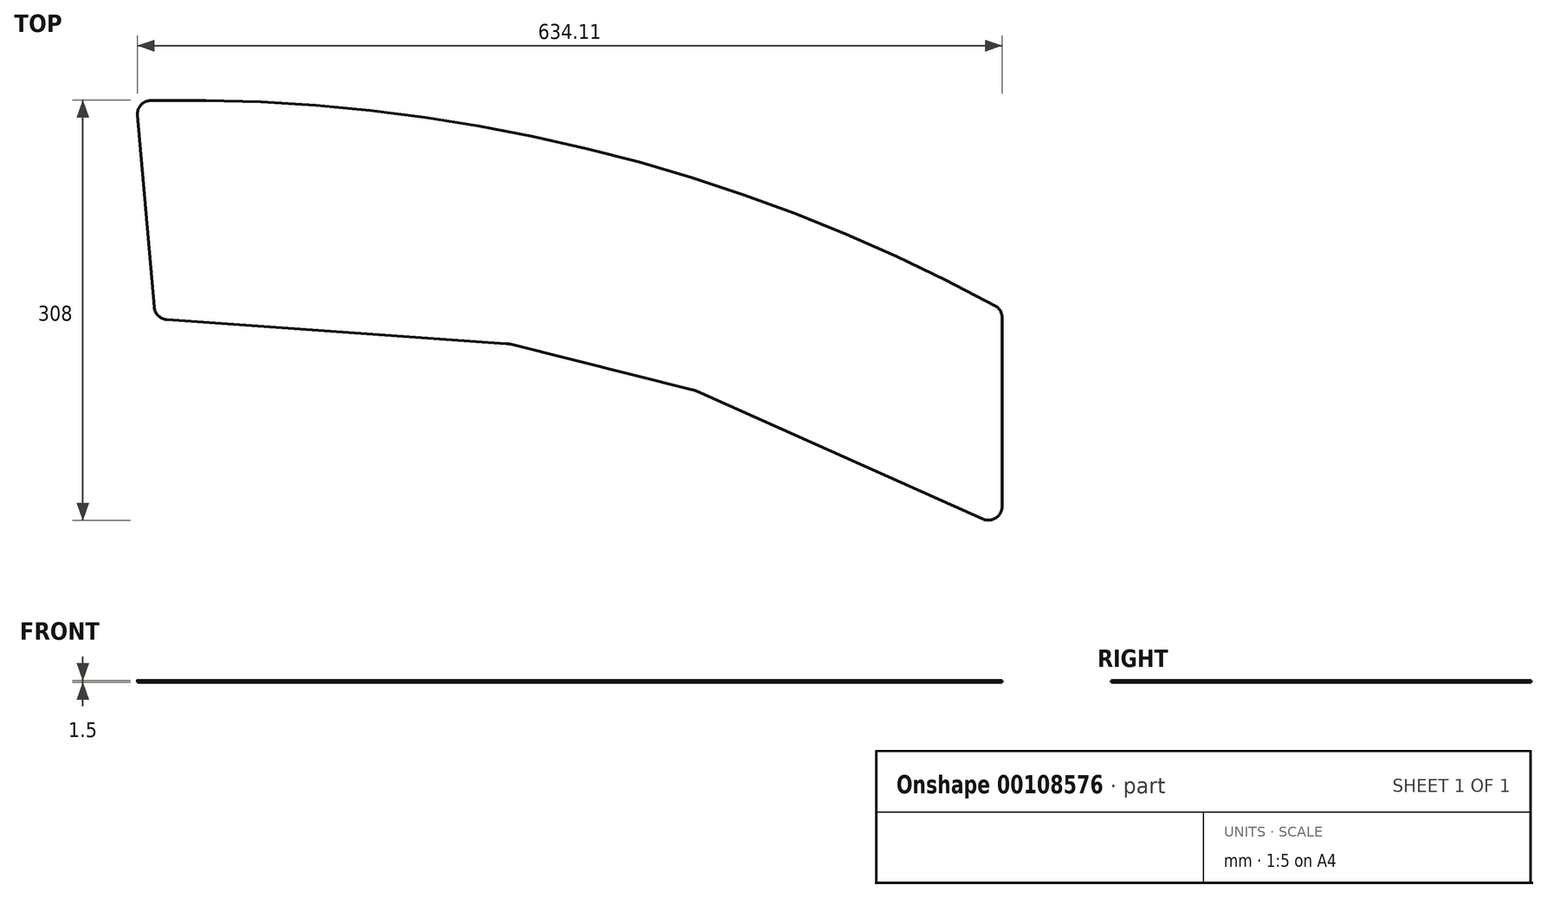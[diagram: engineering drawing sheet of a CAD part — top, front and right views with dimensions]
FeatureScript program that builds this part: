
annotation { "Feature Type Name" : "Feature", "Feature Type Description" : "" }
export const myFeature = defineFeature(function(context is Context, id is Id, definition is map)
    precondition{}
    {
        {
            var Q0;
            Q0=qCreatedBy(makeId("Top.planeOp"),FACE);
            var sketch = newSketch(context, id + "F0", { "sketchPlane" : qUnion([Q0])});
            skLineSegment(sketch, "E0", {"start": v(0, 450) * mm, "end": v(-635, 450) * mm});
            skLineSegment(sketch, "E1", {"start": v(-635, 450) * mm, "end": v(-635, 0) * mm});
            skLineSegment(sketch, "E2", {"start": v(-635, 0) * mm, "end": v(0, 0) * mm});
            skLineSegment(sketch, "E3", {"start": v(0, 0) * mm, "end": v(0, 450) * mm});
            skCircle(sketch, "E4", {"center": v(-600, -900) * mm, "radius": 1070 * mm});
            skCircle(sketch, "E5", {"center": v(-600, -900) * mm, "radius": 1250 * mm});
            skLineSegment(sketch, "E6", {"start": v(-621.03, 189.8) * mm, "end": v(-361.68, 171.41) * mm});
            skLineSegment(sketch, "E7", {"start": v(-361.68, 171.41) * mm, "end": v(-225.87, 137.41) * mm});
            skLineSegment(sketch, "E8", {"start": v(-225.87, 137.41) * mm, "end": v(0, 36.59) * mm});
            skPoint(sketch, "E9", {"position": v(0, 196.59) * mm});
            skLineSegment(sketch, "E10", {"start": v(-621.03, 189.8) * mm, "end": v(-635, 349.5) * mm});
            skSolve(sketch);
        }
        {
            var Q0;
            {var subQ8=sQuery(id+"F0.wireOp",EDGE,"E6");Q0=makeQuery(id+"F0.imprint","IMPRINT",FACE,{"disambiguationData":[TD([[makeQuery(id+"F0.imprint","IMPRINT",EDGE,{"derivedFrom":subQ8}),1.0]])]});}
            extrude(context, id + "F1", {"entities" : qUnion([Q0]), "depth" : 1.5 * mm});
        }
        {
            var Q0;
            Q0=makeQuery(id+"F1.opExtrude","SWEPT_EDGE",EDGE,{"disambiguationData":[OSD([sQuery(id+"F0.wireOp",EDGE,"E3"),sQuery(id+"F0.wireOp",EDGE,"E5")])]});
            var Q1;
            Q1=makeQuery(id+"F1.opExtrude","SWEPT_EDGE",EDGE,{"disambiguationData":[OSD([sQuery(id+"F0.wireOp",EDGE,"E3"),sQuery(id+"F0.wireOp",EDGE,"E4")])]});
            var Q2;
            Q2=makeQuery(id+"F1.opExtrude","SWEPT_EDGE",EDGE,{"disambiguationData":[OSD([sQuery(id+"F0.wireOp",EDGE,"E1"),sQuery(id+"F0.wireOp",EDGE,"E5")])]});
            var Q3;
            Q3=makeQuery(id+"F1.opExtrude","SWEPT_EDGE",EDGE,{"disambiguationData":[OSD([sQuery(id+"F0.wireOp",EDGE,"E1"),sQuery(id+"F0.wireOp",EDGE,"E4")])]});
            var Q4;
            Q4=makeQuery(id+"F1.opExtrude","SWEPT_EDGE",EDGE,{"disambiguationData":[OSD([sQuery(id+"F0.wireOp",EDGE,"E6"),sQuery(id+"F0.wireOp",EDGE,"E10")])]});
            fillet(context, id + "F2", {"entities" : qUnion([Q0, Q1, Q2, Q3, Q4]), "radius" : 10 * mm, "tangentPropagation" : true, "allowEdgeOverflow" : false});
        }
        {
            var Q0;
            Q0=makeQuery(id+"F1.opExtrude","SWEPT_EDGE",EDGE,{"disambiguationData":[OSD([sQuery(id+"F0.wireOp",EDGE,"E6"),sQuery(id+"F0.wireOp",EDGE,"E7")])]});
            var Q1;
            Q1=makeQuery(id+"F1.opExtrude","SWEPT_EDGE",EDGE,{"disambiguationData":[OSD([sQuery(id+"F0.wireOp",EDGE,"E7"),sQuery(id+"F0.wireOp",EDGE,"E8")])]});
            fillet(context, id + "F3", {"entities" : qUnion([Q0, Q1]), "radius" : 20 * mm, "tangentPropagation" : true, "allowEdgeOverflow" : false});
        }
    });
